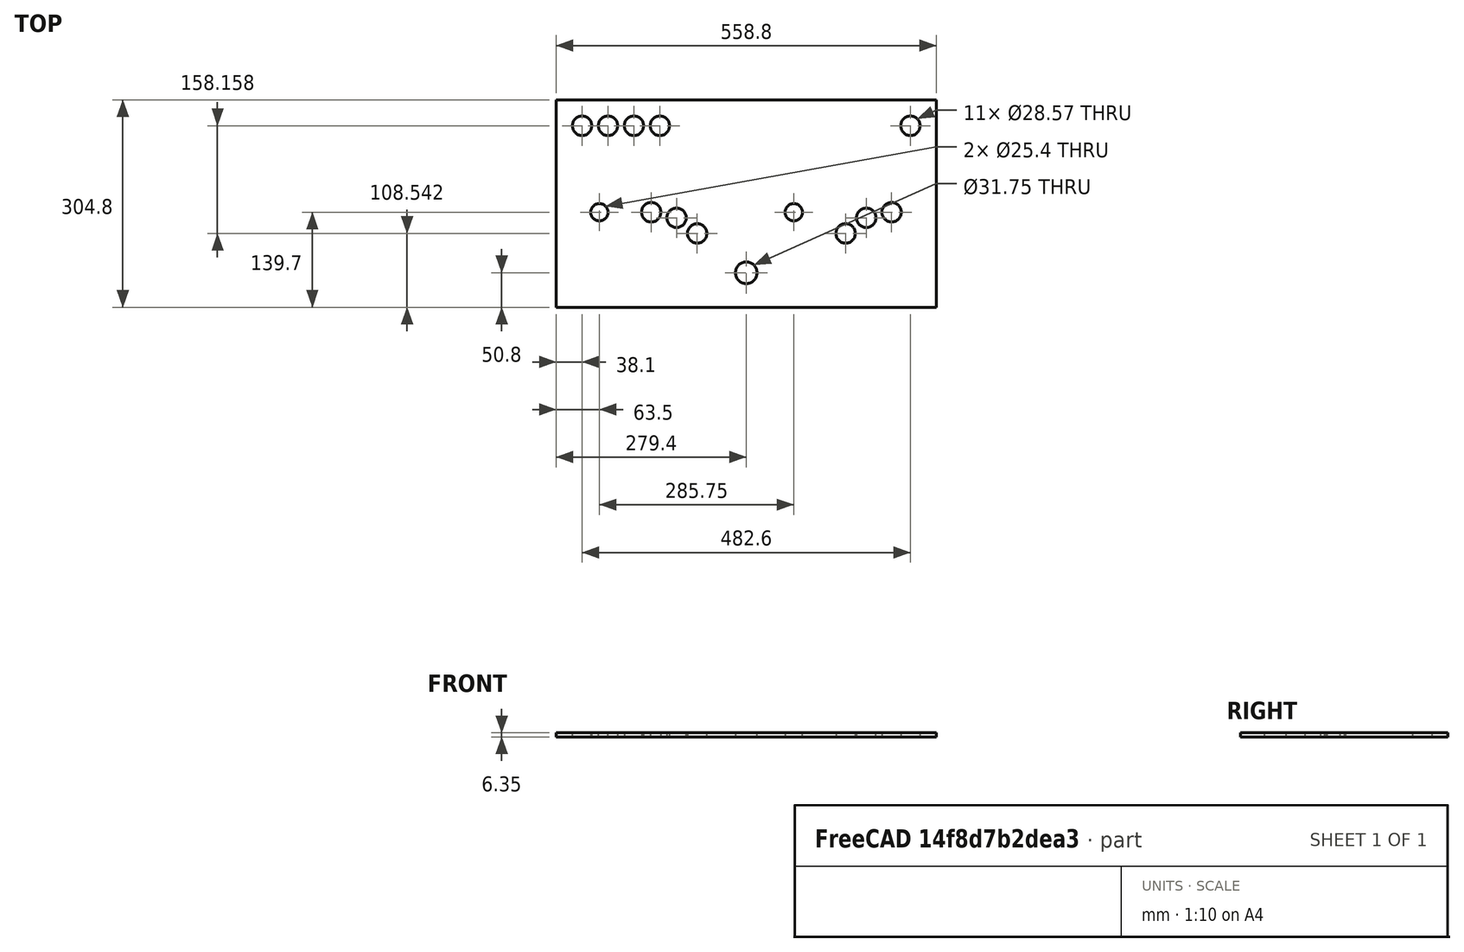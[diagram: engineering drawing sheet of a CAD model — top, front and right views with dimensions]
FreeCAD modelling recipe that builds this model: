
FCSTD DOCUMENT  (FreeCAD 0.18R16146 (Git))
Label: arcade_cabinet
License: All rights reserved
LicenseURL: http://en.wikipedia.org/wiki/All_rights_reserved
objects: Drawing::FeatureViewPython×33, Sketcher::SketchObject×1, PartDesign::Pad×1, PartDesign::Body×1, Drawing::FeatureViewPart×1, Drawing::FeaturePage×1, App::DocumentObjectGroup×1
note: 4 computed .brp shape members not serialized (recipe doc carries the construction recipe); baked Part::Feature solids carry a one-line shape summary decoded from their .brp

FEATURE [Sketcher::SketchObject] Sketch  label="Control Panel Sketch"
  MapMode = 5
  Support = -> [XY_Plane]
  sketch-geometry (20):
    g0: LineSegment StartX=-279.4 StartY=152.4 StartZ=0 EndX=279.4 EndY=152.4 EndZ=0
    g1: LineSegment StartX=279.4 StartY=152.4 StartZ=0 EndX=279.4 EndY=-152.4 EndZ=0
    g2: LineSegment StartX=279.4 StartY=-152.4 StartZ=0 EndX=-279.4 EndY=-152.4 EndZ=0
    g3: LineSegment StartX=-279.4 StartY=-152.4 StartZ=0 EndX=-279.4 EndY=152.4 EndZ=0
    g4: Circle CenterX=-241.3 CenterY=114.3 CenterZ=0 NormalX=0 NormalY=0 NormalZ=1 AngleXU=0 Radius=14.2875
    g5: Circle CenterX=-203.2 CenterY=114.3 CenterZ=0 NormalX=0 NormalY=0 NormalZ=1 AngleXU=0 Radius=14.2875
    g6: Circle CenterX=-127 CenterY=114.3 CenterZ=0 NormalX=0 NormalY=0 NormalZ=1 AngleXU=0 Radius=14.2875
    g7: Circle CenterX=-165.1 CenterY=114.3 CenterZ=0 NormalX=0 NormalY=0 NormalZ=1 AngleXU=0 Radius=14.2875
    g8: Circle CenterX=241.3 CenterY=114.3 CenterZ=0 NormalX=0 NormalY=0 NormalZ=1 AngleXU=0 Radius=14.2875
    g9: Circle CenterX=0 CenterY=-101.6 CenterZ=0 NormalX=0 NormalY=0 NormalZ=1 AngleXU=0 Radius=15.875
    g10: Circle CenterX=-215.9 CenterY=-12.7 CenterZ=0 NormalX=0 NormalY=0 NormalZ=1 AngleXU=0 Radius=12.7
    g11: Circle CenterX=69.85 CenterY=-12.7 CenterZ=0 NormalX=0 NormalY=0 NormalZ=1 AngleXU=0 Radius=12.7
    g12: Circle CenterX=-139.7 CenterY=-12.7 CenterZ=0 NormalX=0 NormalY=0 NormalZ=1 AngleXU=0 Radius=14.2875
    g13: Circle CenterX=-102.485 CenterY=-20.8643 CenterZ=0 NormalX=0 NormalY=0 NormalZ=1 AngleXU=0 Radius=14.2875
    g14: Circle CenterX=-72.1055 CenterY=-43.8576 CenterZ=0 NormalX=0 NormalY=0 NormalZ=1 AngleXU=0 Radius=14.2875
    g15: ArcOfCircle [constr] CenterX=-139.7 CenterY=-101.6 CenterZ=0 NormalX=0 NormalY=0 NormalZ=1 AngleXU=0 Radius=88.9 StartAngle=0.706954 EndAngle=1.5708
    g16: Circle CenterX=146.05 CenterY=-43.8576 CenterZ=0 NormalX=0 NormalY=0 NormalZ=1 AngleXU=0 Radius=14.2875
    g17: Circle CenterX=176.43 CenterY=-20.8643 CenterZ=0 NormalX=0 NormalY=0 NormalZ=1 AngleXU=0 Radius=14.2875
    g18: Circle CenterX=213.645 CenterY=-12.7 CenterZ=0 NormalX=0 NormalY=0 NormalZ=1 AngleXU=0 Radius=14.2875
    g19: ArcOfCircle [constr] CenterX=213.645 CenterY=-101.6 CenterZ=0 NormalX=0 NormalY=0 NormalZ=1 AngleXU=0 Radius=88.9 StartAngle=1.5708 EndAngle=2.43464
  constraints (60):
    c: Coincident(g0,g1)
    c: Coincident(g1,g2)
    c: Coincident(g2,g3)
    c: Coincident(g3,g0)
    c: Horizontal(g0)
    c: Vertical(g1)
    c: Vertical(g3)
    c: Equal(g1,g3)
    c: DistanceX(g0,g0) = 558.8  'Panel Length'
    c: DistanceY(g1,g1) = 304.8  'Panel Width'
    c: Distance(g-1,g1) = 279.4
    c: Distance(g-1,g0) = 152.4
    c: Diameter(g4) = 28.575  'PButton Diameter 1'
    c: Equal(g4,g5) = 28.575  'PButton Diameter 2'
    c: Equal(g4,g7) = 28.575  'PButton Diameter 3'
    c: Equal(g7,g6) = 28.575  'PButton Diameter 4'
    c: DistanceX(g4,g5) = 38.1  'PButton HAlign 1'
    c: DistanceX(g5,g7) = 38.1  'PButton HAlign 2'
    c: DistanceX(g7,g6) = 38.1  'PButton HAlign 3'
    c: DistanceY(g4,g5) = 0  'PButton VAlign 1'
    c: DistanceY(g6,g5) = 0  'PButton VAlign 2'
    c: DistanceY(g7,g6) = 0  'PButton VAlign 3'
    c: DistanceY(g4,g0) = 38.1  'PButtons from Top'
    c: DistanceX(g0,g4) = 38.1  'PButtons from Left'
    c: Diameter(g8) = 28.575  'Tab Button Diameter'
    c: DistanceY(g8,g0) = 38.1  'Tab from Top'
    c: DistanceX(g8,g0) = 38.1  'Tab from Right'
    c: PointOnObject(g9,g-2)  'SPNR_CNTR'
    c: Diameter(g9) = 31.75  'SPNR_Diam'
    c: Diameter(g10) = 25.4  'JSTK1_Diam'
    c: DistanceX(g0,g10) = 63.5  'JSTK1_HDist'
    c: DistanceY(g2,g10) = 139.7  'JSTK1_VDist'
    c: DistanceY(g2,g9) = 50.8  'SPNR_VDist'
    c: DistanceY(g11,g10) = 0  'JSTK2_VAlign'
    c: DistanceX(g11,g1) = 209.55  'JSTK2_HDist'
    c: Diameter(g11) = 25.4  'JSTK2_Diam'
    c: Diameter(g12) = 28.575  'P1_Button1_Diam'
    c: DistanceX(g10,g12) = 76.2  'P1_Button1_to_JSTK1_HDist'
    c: DistanceY(g12,g10) = 0  'P1_Button1_to_JSTK1_VDist'
    c: Equal(g13,g12)  'P1_Button2_Diam'
    c: Equal(g12,g14)  'P1_Button3_Diam'
    c: Coincident(g15,g12)  'P1_Button1_Center'
    c: Coincident(g15,g14)  'P1_Button3_Center'
    c: DistanceX(g12,g15) = 0  'P1_Button_to_Arc_Center'
    c: DistanceY(g2,g15) = 50.8  'Arc_Center_to_Panel_Bottom'
    c: PointOnObject(g13,g15)  'P1_Button2_Arc'
    c: Distance(g13,g12) = 38.1  'P1_Button1_to_P1_Button2'
    c: Distance(g14,g13) = 38.1  'P1_Button2_to_P1_Button3'
    c: Diameter(g16) = 28.575  'P1_Button1_Diam'
    c: Equal(g17,g16)  'P1_Button2_Diam'
    c: Equal(g16,g18)  'P1_Button3_Diam'
    c: Coincident(g19,g16)  'P2_Button1_Center'
    c: Coincident(g19,g18)  'P2_Button3_Center'
    c: PointOnObject(g17,g19)  'P2_Button2_Arc'
    c: Distance(g17,g16) = 38.1  'P2_Button1_to_P2_Button2'
    c: Distance(g18,g17) = 38.1  'P2_Button2_to_P2_Button3'
    c: DistanceY(g1,g19) = 50.8  'P2_Button_Arc_Vdist'
    c: DistanceX(g19,g18) = 0  'P2_Button3_to_Arc_Center_HDist'
    c: DistanceX(g11,g16) = 76.2  'P2_Button1_to_JSTK2_Hdist'
    c: DistanceY(g18,g11) = 0  'P2_Button3_to_JSTK2_Vdist'
FEATURE [PartDesign::Pad] Pad  label="Control Panel Pad"
  Length = 6.35
  Length2 = 100.076
  Profile = -> Sketch
  Type = 0
FEATURE [PartDesign::Body] Body  label="Control Panel Body"
  Group = -> [Sketch,Pad]
  Origin = -> Origin
  Tip = -> Pad
FEATURE [Drawing::FeatureViewPart] Ortho  label="Control Panel Ortho View"
  Direction = (0,0,1)
  HiddenWidth = 0.15
  LineWidth = 0.35
  Rotation = 0
  Scale = 0.25
  ShowHiddenLines = false
  ShowSmoothLines = false
  Source = -> Body
  Tolerance = 0.05
  ViewResult = <g id="Control Panel Ortho View"\n   transform="rotate(0,148.5,81.5) translate(148.5,81.5) scale(0.25,0.25)"\n  >\n<g   fill="none"\n   stroke="rgb(0, 0, 0)"\n   stroke-linecap="butt"\n   stroke-linejoin="miter"\n   stroke-width="1.400000"\n   transform="scale(1,-1)"\n  >\n<path id= "1" d=" M -279.4 152.4 L 279.4 152.4 " />\n<path id= "2" d=" M 279.4 152.4 L 279.4 -152.4 " />\n<path id= "3" d=" M 279.4 -152.4 L -279.4 -152.4 " />\n<path id= "4" d=" M -279.4 -152.4 L -279.4 152.4 " />\n<circle cx ="0" cy ="-101.6" r ="15.875" /><circle cx ="-72.1055" cy ="-43.8576" r ="14.2875" /><circle cx ="146.05" cy ="-43.8576" r ="14.2875" /><circle cx ="176.43" cy ="-20.8643" r ="14.2875" /><circle cx ="-102.485" cy ="-20.8643" r ="14.2875" /><circle cx ="-139.7" cy ="-12.7" r ="14.2875" /><circle cx ="213.645" cy ="-12.7" r ="14.2875" /><circle cx ="-127" cy ="114.3" r ="14.2875" /><circle cx ="241.3" cy ="114.3" r ="14.2875" /><circle cx ="-165.1" cy ="114.3" r ="14.2875" /><circle cx ="-241.3" cy ="114.3" r ="14.2875" /><circle cx ="-203.2" cy ="114.3" r ="14.2875" /><circle cx ="69.85" cy ="-12.7" r ="12.7" /><circle cx ="-215.9" cy ="-12.7" r ="12.7" /></g>\n</g>
  Visible = true
  X = 148.5
  Y = 81.5
FEATURE [Drawing::FeatureViewPython] dim001  label="Panel Width"  # drawing view (typed FeaturePython)
  Rotation = 0
  ViewResult = <g> \n  <line x1="76.650000" y1="119.600000" x2="57.586698" y2="119.600000" style="stroke:rgb(0,0,255);stroke-width:0.50" />\n<line x1="76.650000" y1="43.400000" x2="57.586698" y2="43.400000" style="stroke:rgb(0,0,255);stroke-width:0.50" />\n<line x1="58.586698" y1="119.600000" x2="58.586698" y2="43.400000" style="stroke:rgb(0,0,255);stroke-width:0.50" /> \n  <polygon points="58.586698,43.400000 57.586698,44.900000 58.586698,45.400000 59.586698,44.900000" style="fill:rgb(0,0,255);stroke:rgb(0,0,255);stroke-width:0" /><polygon points="58.586698,119.600000 59.586698,118.100000 58.586698,117.600000 57.586698,118.100000" style="fill:rgb(0,0,255);stroke:rgb(0,0,255);stroke-width:0" /> \n  <text x="56.586698" y="81.500000" font-family="inherit" font-size="3.6" fill="rgb(0,0,255)" text-anchor="middle" transform="rotate(-90.000000 56.586698,81.500000)" >12</text> </g>
  Visible = true
  X = 0
  Y = 0
  arrowL1 = 1.5
  arrowL2 = 0.5
  arrowW = 2
  arrow_scheme = 0
  autoPlaceOffset = 2
  autoPlaceText = true
  click1_x = 58.5867
  click1_y = 76.756
  click2_x = 58.5867
  click2_y = 76.756
  comma_decimal_place = false
  dimension_line_overshoot = 1
  gap_datum_points = 2
  halfDimension_linear = false
  lineColor = rgb(0,0,255)
  strokeWidth = 0.5
  textFormat_linear = %(value)3.3f
  textRenderer_color = rgb(0,0,255)
  textRenderer_family = inherit
  textRenderer_size = 3.6
  unit_custom_scale = 1
  unit_scheme = 2
FEATURE [Drawing::FeatureViewPython] dim002  label="Panel Length"  # drawing view (typed FeaturePython)
  Rotation = 0
  ViewResult = <g> \n  <line x1="78.650000" y1="41.400000" x2="78.650000" y2="26.439340" style="stroke:rgb(0,0,255);stroke-width:0.50" />\n<line x1="218.350000" y1="41.400000" x2="218.350000" y2="26.439340" style="stroke:rgb(0,0,255);stroke-width:0.50" />\n<line x1="78.650000" y1="27.439340" x2="218.350000" y2="27.439340" style="stroke:rgb(0,0,255);stroke-width:0.50" /> \n  <polygon points="218.350000,27.439340 216.850000,26.439340 216.350000,27.439340 216.850000,28.439340" style="fill:rgb(0,0,255);stroke:rgb(0,0,255);stroke-width:0" /><polygon points="78.650000,27.439340 80.150000,28.439340 80.650000,27.439340 80.150000,26.439340" style="fill:rgb(0,0,255);stroke:rgb(0,0,255);stroke-width:0" /> \n  <text x="148.500000" y="25.439340" font-family="inherit" font-size="3.6" fill="rgb(0,0,255)" text-anchor="middle" transform="rotate(0.000000 148.500000,25.439340)" >22</text> </g>
  Visible = true
  X = 0
  Y = 0
  arrowL1 = 1.5
  arrowL2 = 0.5
  arrowW = 2
  arrow_scheme = 0
  autoPlaceOffset = 2
  autoPlaceText = true
  click1_x = 102.712
  click1_y = 27.4393
  click2_x = 102.712
  click2_y = 27.4393
  comma_decimal_place = false
  dimension_line_overshoot = 1
  gap_datum_points = 2
  halfDimension_linear = false
  lineColor = rgb(0,0,255)
  strokeWidth = 0.5
  textFormat_linear = %(value)3.3f
  textRenderer_color = rgb(0,0,255)
  textRenderer_family = inherit
  textRenderer_size = 3.6
  unit_custom_scale = 1
  unit_scheme = 2
FEATURE [Drawing::FeatureViewPython] dim004  label="Coin Button HDist to Panel Edge"  # drawing view (typed FeaturePython)
  Rotation = 0
  ViewResult = <g> \n  <line x1="88.175000" y1="58.496875" x2="88.175000" y2="64.914175" style="stroke:rgb(0,0,255);stroke-width:0.50" />\n<line x1="78.650000" y1="45.400000" x2="78.650000" y2="64.914175" style="stroke:rgb(0,0,255);stroke-width:0.50" />\n<line x1="88.175000" y1="63.914175" x2="78.650000" y2="63.914175" style="stroke:rgb(0,0,255);stroke-width:0.50" /> \n  <polygon points="78.650000,63.914175 80.150000,64.914175 80.650000,63.914175 80.150000,62.914175" style="fill:rgb(0,0,255);stroke:rgb(0,0,255);stroke-width:0" /><polygon points="88.175000,63.914175 86.675000,62.914175 86.175000,63.914175 86.675000,64.914175" style="fill:rgb(0,0,255);stroke:rgb(0,0,255);stroke-width:0" /> \n  <text x="83.412500" y="61.914175" font-family="inherit" font-size="3.6" fill="rgb(0,0,255)" text-anchor="middle" transform="rotate(0.000000 83.412500,61.914175)" >1.5</text> </g>
  Visible = true
  X = 0
  Y = 0
  arrowL1 = 1.5
  arrowL2 = 0.5
  arrowW = 2
  arrow_scheme = 0
  autoPlaceOffset = 2
  autoPlaceText = true
  click1_x = 85.5208
  click1_y = 63.9142
  click2_x = 85.5208
  click2_y = 63.9142
  comma_decimal_place = false
  dimension_line_overshoot = 1
  gap_datum_points = 2
  halfDimension_linear = false
  lineColor = rgb(0,0,255)
  strokeWidth = 0.5
  textFormat_linear = %(value)3.3f
  textRenderer_color = rgb(0,0,255)
  textRenderer_family = inherit
  textRenderer_size = 3.6
  unit_custom_scale = 1
  unit_scheme = 2
FEATURE [Drawing::FeatureViewPython] dim005  label="Coin Button VDist to Panel Edge"  # drawing view (typed FeaturePython)
  Rotation = 0
  ViewResult = <g> \n  <line x1="82.603125" y1="52.925000" x2="70.422058" y2="52.925000" style="stroke:rgb(0,0,255);stroke-width:0.50" />\n<line x1="76.650000" y1="43.400000" x2="70.422058" y2="43.400000" style="stroke:rgb(0,0,255);stroke-width:0.50" />\n<line x1="71.422058" y1="52.925000" x2="71.422058" y2="43.400000" style="stroke:rgb(0,0,255);stroke-width:0.50" /> \n  <polygon points="71.422058,43.400000 70.422058,44.900000 71.422058,45.400000 72.422058,44.900000" style="fill:rgb(0,0,255);stroke:rgb(0,0,255);stroke-width:0" /><polygon points="71.422058,52.925000 72.422058,51.425000 71.422058,50.925000 70.422058,51.425000" style="fill:rgb(0,0,255);stroke:rgb(0,0,255);stroke-width:0" /> \n  <text x="69.422058" y="48.162500" font-family="inherit" font-size="3.6" fill="rgb(0,0,255)" text-anchor="middle" transform="rotate(-90.000000 69.422058,48.162500)" >1.5</text> </g>
  Visible = true
  X = 0
  Y = 0
  arrowL1 = 1.5
  arrowL2 = 0.5
  arrowW = 2
  arrow_scheme = 0
  autoPlaceOffset = 2
  autoPlaceText = true
  click1_x = 71.4221
  click1_y = 52.2878
  click2_x = 71.4221
  click2_y = 52.2878
  comma_decimal_place = false
  dimension_line_overshoot = 1
  gap_datum_points = 2
  halfDimension_linear = false
  lineColor = rgb(0,0,255)
  strokeWidth = 0.5
  textFormat_linear = %(value)3.3f
  textRenderer_color = rgb(0,0,255)
  textRenderer_family = inherit
  textRenderer_size = 3.6
  unit_custom_scale = 1
  unit_scheme = 2
FEATURE [Drawing::FeatureViewPython] dim006  label="Coin Button to P1 Button HDist"  # drawing view (typed FeaturePython)
  Rotation = 0
  ViewResult = <g> \n  <line x1="88.175000" y1="54.925000" x2="88.175000" y2="64.996578" style="stroke:rgb(0,0,255);stroke-width:0.50" />\n<line x1="97.700000" y1="54.925000" x2="97.700000" y2="64.996578" style="stroke:rgb(0,0,255);stroke-width:0.50" />\n<line x1="88.175000" y1="63.996578" x2="97.700000" y2="63.996578" style="stroke:rgb(0,0,255);stroke-width:0.50" /> \n  <polygon points="97.700000,63.996578 96.200000,62.996578 95.700000,63.996578 96.200000,64.996578" style="fill:rgb(0,0,255);stroke:rgb(0,0,255);stroke-width:0" /><polygon points="88.175000,63.996578 89.675000,64.996578 90.175000,63.996578 89.675000,62.996578" style="fill:rgb(0,0,255);stroke:rgb(0,0,255);stroke-width:0" /> \n  <text x="92.937500" y="61.996578" font-family="inherit" font-size="3.6" fill="rgb(0,0,255)" text-anchor="middle" transform="rotate(0.000000 92.937500,61.996578)" >1.5</text> </g>
  Visible = true
  X = 0
  Y = 0
  arrowL1 = 1.5
  arrowL2 = 0.5
  arrowW = 2
  arrow_scheme = 0
  autoPlaceOffset = 2
  autoPlaceText = true
  click1_x = 98.1851
  click1_y = 63.9966
  click2_x = 98.1851
  click2_y = 63.9966
  comma_decimal_place = false
  dimension_line_overshoot = 1
  gap_datum_points = 2
  halfDimension_linear = false
  lineColor = rgb(0,0,255)
  strokeWidth = 0.5
  textFormat_linear = %(value)3.3f
  textRenderer_color = rgb(0,0,255)
  textRenderer_family = inherit
  textRenderer_size = 3.6
  unit_custom_scale = 1
  unit_scheme = 2
FEATURE [Drawing::FeatureViewPython] dim008  label="JSTK1 HDist to Panel"  # drawing view (typed FeaturePython)
  Rotation = 0
  ViewResult = <g> \n  <line x1="94.525000" y1="89.850000" x2="94.525000" y2="100.695034" style="stroke:rgb(0,0,255);stroke-width:0.50" />\n<line x1="78.650000" y1="117.600000" x2="78.650000" y2="98.695034" style="stroke:rgb(0,0,255);stroke-width:0.50" />\n<line x1="94.525000" y1="99.695034" x2="78.650000" y2="99.695034" style="stroke:rgb(0,0,255);stroke-width:0.50" /> \n  <polygon points="78.650000,99.695034 80.150000,100.695034 80.650000,99.695034 80.150000,98.695034" style="fill:rgb(0,0,255);stroke:rgb(0,0,255);stroke-width:0" /><polygon points="94.525000,99.695034 93.025000,98.695034 92.525000,99.695034 93.025000,100.695034" style="fill:rgb(0,0,255);stroke:rgb(0,0,255);stroke-width:0" /> \n  <text x="86.587500" y="97.695034" font-family="inherit" font-size="3.6" fill="rgb(0,0,255)" text-anchor="middle" transform="rotate(0.000000 86.587500,97.695034)" >2.5</text> </g>
  Visible = true
  X = 0
  Y = 0
  arrowL1 = 1.5
  arrowL2 = 0.5
  arrowW = 2
  arrow_scheme = 0
  autoPlaceOffset = 2
  autoPlaceText = true
  click1_x = 85.952
  click1_y = 99.695
  click2_x = 85.952
  click2_y = 99.695
  comma_decimal_place = false
  dimension_line_overshoot = 1
  gap_datum_points = 2
  halfDimension_linear = false
  lineColor = rgb(0,0,255)
  strokeWidth = 0.5
  textFormat_linear = %(value)3.3f
  textRenderer_color = rgb(0,0,255)
  textRenderer_family = inherit
  textRenderer_size = 3.6
  unit_custom_scale = 1
  unit_scheme = 2
FEATURE [Drawing::FeatureViewPython] dim009  label="JSTK1 VDist to Panel"  # drawing view (typed FeaturePython)
  Rotation = 0
  ViewResult = <g> \n  <line x1="89.350000" y1="84.675000" x2="68.879697" y2="84.675000" style="stroke:rgb(0,0,255);stroke-width:0.50" />\n<line x1="76.650000" y1="119.600000" x2="68.879697" y2="119.600000" style="stroke:rgb(0,0,255);stroke-width:0.50" />\n<line x1="69.879697" y1="84.675000" x2="69.879697" y2="119.600000" style="stroke:rgb(0,0,255);stroke-width:0.50" /> \n  <polygon points="69.879697,119.600000 70.879697,118.100000 69.879697,117.600000 68.879697,118.100000" style="fill:rgb(0,0,255);stroke:rgb(0,0,255);stroke-width:0" /><polygon points="69.879697,84.675000 68.879697,86.175000 69.879697,86.675000 70.879697,86.175000" style="fill:rgb(0,0,255);stroke:rgb(0,0,255);stroke-width:0" /> \n  <text x="67.879697" y="102.137500" font-family="inherit" font-size="3.6" fill="rgb(0,0,255)" text-anchor="middle" transform="rotate(-90.000000 67.879697,102.137500)" >5.5</text> </g>
  Visible = true
  X = 0
  Y = 0
  arrowL1 = 1.5
  arrowL2 = 0.5
  arrowW = 2
  arrow_scheme = 0
  autoPlaceOffset = 2
  autoPlaceText = true
  click1_x = 69.8797
  click1_y = 94.1047
  click2_x = 69.8797
  click2_y = 94.1047
  comma_decimal_place = false
  dimension_line_overshoot = 1
  gap_datum_points = 2
  halfDimension_linear = false
  lineColor = rgb(0,0,255)
  strokeWidth = 0.5
  textFormat_linear = %(value)3.3f
  textRenderer_color = rgb(0,0,255)
  textRenderer_family = inherit
  textRenderer_size = 3.6
  unit_custom_scale = 1
  unit_scheme = 2
FEATURE [Drawing::FeatureViewPython] dim010  label="P1 Button1 to JSTK1 HDist"  # drawing view (typed FeaturePython)
  Rotation = 0
  ViewResult = <g> \n  <line x1="94.525000" y1="86.675000" x2="94.525000" y2="100.684233" style="stroke:rgb(0,0,255);stroke-width:0.50" />\n<line x1="113.575000" y1="86.675000" x2="113.575000" y2="100.684233" style="stroke:rgb(0,0,255);stroke-width:0.50" />\n<line x1="94.525000" y1="99.684233" x2="113.575000" y2="99.684233" style="stroke:rgb(0,0,255);stroke-width:0.50" /> \n  <polygon points="113.575000,99.684233 112.075000,98.684233 111.575000,99.684233 112.075000,100.684233" style="fill:rgb(0,0,255);stroke:rgb(0,0,255);stroke-width:0" /><polygon points="94.525000,99.684233 96.025000,100.684233 96.525000,99.684233 96.025000,98.684233" style="fill:rgb(0,0,255);stroke:rgb(0,0,255);stroke-width:0" /> \n  <text x="104.050000" y="97.684233" font-family="inherit" font-size="3.6" fill="rgb(0,0,255)" text-anchor="middle" transform="rotate(0.000000 104.050000,97.684233)" >3</text> </g>
  Visible = true
  X = 0
  Y = 0
  arrowL1 = 1.5
  arrowL2 = 0.5
  arrowW = 2
  arrow_scheme = 0
  autoPlaceOffset = 2
  autoPlaceText = true
  click1_x = 113.952
  click1_y = 99.6842
  click2_x = 113.952
  click2_y = 99.6842
  comma_decimal_place = false
  dimension_line_overshoot = 1
  gap_datum_points = 2
  halfDimension_linear = false
  lineColor = rgb(0,0,255)
  strokeWidth = 0.5
  textFormat_linear = %(value)3.3f
  textRenderer_color = rgb(0,0,255)
  textRenderer_family = inherit
  textRenderer_size = 3.6
  unit_custom_scale = 1
  unit_scheme = 2
FEATURE [Drawing::FeatureViewPython] dia001  label="Coin Button Diameter"  # drawing view (typed FeaturePython)
  Rotation = 0
  ViewResult = <g>  <circle cx ="88.175000" cy ="52.925000" r="0.250000" stroke="none" fill="rgb(0,0,255)" /> \n<line x1="88.001472" y1="40.209550" x2="88.223741" y2="56.496542" style="stroke:rgb(0,0,255);stroke-width:0.50" />\n<polygon points="88.126259,49.353458 87.146821,50.866964 88.153551,51.353271 89.146635,50.839672" style="fill:rgb(0,0,255);stroke:rgb(0,0,255);stroke-width:0" />\n<polygon points="88.223741,56.496542 89.203179,54.983036 88.196449,54.496729 87.203365,55.010328" style="fill:rgb(0,0,255);stroke:rgb(0,0,255);stroke-width:0" />\n<line x1="88.001472" y1="40.209550" x2="96.962458" y2="40.209550" style="stroke:rgb(0,0,255);stroke-width:0.50" />\n<text x="92.481965" y="38.209550" font-family="inherit" font-size="3.6" fill="rgb(0,0,255)" text-anchor="middle" transform="rotate(0.000000 92.481965,38.209550)" >Ø1.125</text> </g>
  Visible = true
  X = 0
  Y = 0
  arrowL1 = 1.5
  arrowL2 = 0.5
  arrowW = 2
  arrow_scheme = 0
  autoPlaceOffset = 2
  autoPlaceText = true
  centerPointDia = 0.5
  click1_x = 88.0015
  click1_y = 40.2095
  click2_x = 96.9625
  click2_y = 40.4393
  click3_x = 96.9625
  click3_y = 40.4393
  comma_decimal_place = false
  lineColor = rgb(0,0,255)
  strokeWidth = 0.5
  textFormat_circular = Ø%(value)3.3f
  textRenderer_color = rgb(0,0,255)
  textRenderer_family = inherit
  textRenderer_size = 3.6
  unit_custom_scale = 1
  unit_scheme = 2
FEATURE [Drawing::FeatureViewPython] dia002  label="JSTK1 Diameter"  # drawing view (typed FeaturePython)
  Rotation = 0
  ViewResult = <g>  <circle cx ="94.525000" cy ="84.675000" r="0.250000" stroke="none" fill="rgb(0,0,255)" /> \n<line x1="94.894538" y1="77.891643" x2="94.352291" y2="87.845299" style="stroke:rgb(0,0,255);stroke-width:0.50" />\n<polygon points="94.697709,81.504701 93.617595,82.948083 94.588916,83.501740 95.614634,83.056876" style="fill:rgb(0,0,255);stroke:rgb(0,0,255);stroke-width:0" />\n<polygon points="94.352291,87.845299 95.432405,86.401917 94.461084,85.848260 93.435366,86.293124" style="fill:rgb(0,0,255);stroke:rgb(0,0,255);stroke-width:0" />\n<line x1="94.894538" y1="77.891643" x2="99.260146" y2="77.891643" style="stroke:rgb(0,0,255);stroke-width:0.50" />\n<text x="97.077342" y="75.891643" font-family="inherit" font-size="3.6" fill="rgb(0,0,255)" text-anchor="middle" transform="rotate(0.000000 97.077342,75.891643)" >Ø1</text> </g>
  Visible = true
  X = 0
  Y = 0
  arrowL1 = 1.5
  arrowL2 = 0.5
  arrowW = 2
  arrow_scheme = 0
  autoPlaceOffset = 2
  autoPlaceText = true
  centerPointDia = 0.5
  click1_x = 94.8945
  click1_y = 77.8916
  click2_x = 99.2601
  click2_y = 78.1214
  click3_x = 99.2601
  click3_y = 78.1214
  comma_decimal_place = false
  lineColor = rgb(0,0,255)
  strokeWidth = 0.5
  textFormat_circular = Ø%(value)3.3f
  textRenderer_color = rgb(0,0,255)
  textRenderer_family = inherit
  textRenderer_size = 3.6
  unit_custom_scale = 1
  unit_scheme = 2
FEATURE [Drawing::FeatureViewPython] dia003  label="P1 Button1 Diameter"  # drawing view (typed FeaturePython)
  Rotation = 0
  ViewResult = <g>  <circle cx ="113.575000" cy ="84.675000" r="0.250000" stroke="none" fill="rgb(0,0,255)" /> \n<line x1="113.590548" y1="77.646686" x2="113.567098" y2="88.246866" style="stroke:rgb(0,0,255);stroke-width:0.50" />\n<polygon points="113.582902,81.103134 112.579586,82.600918 113.578477,83.103129 114.579581,82.605342" style="fill:rgb(0,0,255);stroke:rgb(0,0,255);stroke-width:0" />\n<polygon points="113.567098,88.246866 114.570414,86.749082 113.571523,86.246871 112.570419,86.744658" style="fill:rgb(0,0,255);stroke:rgb(0,0,255);stroke-width:0" />\n<line x1="113.590548" y1="77.646686" x2="118.158000" y2="77.646686" style="stroke:rgb(0,0,255);stroke-width:0.50" />\n<text x="115.874274" y="75.646686" font-family="inherit" font-size="3.6" fill="rgb(0,0,255)" text-anchor="middle" transform="rotate(0.000000 115.874274,75.646686)" >Ø1.125</text> </g>
  Visible = true
  X = 0
  Y = 0
  arrowL1 = 1.5
  arrowL2 = 0.5
  arrowW = 2
  arrow_scheme = 0
  autoPlaceOffset = 2
  autoPlaceText = true
  centerPointDia = 0.5
  click1_x = 113.591
  click1_y = 77.6467
  click2_x = 118.158
  click2_y = 78.0439
  click3_x = 118.158
  click3_y = 78.0439
  comma_decimal_place = false
  lineColor = rgb(0,0,255)
  strokeWidth = 0.5
  textFormat_circular = Ø%(value)3.3f
  textRenderer_color = rgb(0,0,255)
  textRenderer_family = inherit
  textRenderer_size = 3.6
  unit_custom_scale = 1
  unit_scheme = 2
FEATURE [Drawing::FeatureViewPython] dimStack001  label="P1 Button1 to P1 Button3"  # drawing view (typed FeaturePython)
  Rotation = 0
  ViewResult = <g> <line x1="113.575000" y1="86.675001" x2="113.575000" y2="110.228830" style="stroke:rgb(0,0,255);stroke-width:0.50" />\n<line x1="130.473625" y1="94.464401" x2="130.473625" y2="110.228830" style="stroke:rgb(0,0,255);stroke-width:0.50" />\n<line x1="113.575000" y1="109.228830" x2="130.473625" y2="109.228830" style="stroke:rgb(0,0,255);stroke-width:0.50" />\n<polygon points="113.575000,109.228830 115.075000,110.228830 115.575000,109.228830 115.075000,108.228830" style="fill:rgb(0,0,255);stroke:rgb(0,0,255);stroke-width:0" />\n<polygon points="130.473625,109.228830 128.973625,108.228830 128.473625,109.228830 128.973625,110.228830" style="fill:rgb(0,0,255);stroke:rgb(0,0,255);stroke-width:0" />\n<text x="122.024313" y="107.228830" font-family="inherit" font-size="3.6" fill="rgb(0,0,255)" text-anchor="middle" transform="rotate(0.000000 122.024313,107.228830)" >2.661</text> </g> 
  Visible = true
  X = 0
  Y = 0
  arrowL1 = 1.5
  arrowL2 = 0.5
  arrowW = 2
  arrow_scheme = 0
  autoPlaceOffset = 2
  click1_x = 117.672
  click1_y = 109.229
  comma_decimal_place = false
  dimension_line_overshoot = 1
  gap_datum_points = 2
  lineColor = rgb(0,0,255)
  stack_offset = 7
  stack_offset0 = 0
  strokeWidth = 0.5
  textFormat_linear = %(value)3.3f
  textRenderer_color = rgb(0,0,255)
  textRenderer_family = inherit
  textRenderer_size = 3.6
  unit_custom_scale = 1
  unit_scheme = 2
FEATURE [Drawing::FeatureViewPython] dimStack002  label="P1 Button1 to P1 Button2"  # drawing view (typed FeaturePython)
  Rotation = 0
  ViewResult = <g> <line x1="122.878750" y1="88.716076" x2="122.878750" y2="100.730671" style="stroke:rgb(0,0,255);stroke-width:0.50" />\n<line x1="113.575000" y1="86.675001" x2="113.575000" y2="100.730671" style="stroke:rgb(0,0,255);stroke-width:0.50" />\n<line x1="122.878750" y1="99.730671" x2="113.575000" y2="99.730671" style="stroke:rgb(0,0,255);stroke-width:0.50" />\n<polygon points="122.878750,99.730671 121.378750,98.730671 120.878750,99.730671 121.378750,100.730671" style="fill:rgb(0,0,255);stroke:rgb(0,0,255);stroke-width:0" />\n<polygon points="113.575000,99.730671 115.075000,100.730671 115.575000,99.730671 115.075000,98.730671" style="fill:rgb(0,0,255);stroke:rgb(0,0,255);stroke-width:0" />\n<text x="118.226875" y="97.730671" font-family="inherit" font-size="3.6" fill="rgb(0,0,255)" text-anchor="middle" transform="rotate(0.000000 118.226875,97.730671)" >1.465</text> </g> 
  Visible = true
  X = 0
  Y = 0
  arrowL1 = 1.5
  arrowL2 = 0.5
  arrowW = 2
  arrow_scheme = 0
  autoPlaceOffset = 2
  click1_x = 122.157
  click1_y = 99.7307
  comma_decimal_place = false
  dimension_line_overshoot = 1
  gap_datum_points = 2
  lineColor = rgb(0,0,255)
  stack_offset = 7
  stack_offset0 = 0
  strokeWidth = 0.5
  textFormat_linear = %(value)3.3f
  textRenderer_color = rgb(0,0,255)
  textRenderer_family = inherit
  textRenderer_size = 3.6
  unit_custom_scale = 1
  unit_scheme = 2
FEATURE [Drawing::FeatureViewPython] centerLines001  label="Panel Center Left"  # drawing view (typed FeaturePython)
  Rotation = 0
  ViewResult = <g transform="scale(0.250000,0.250000)" stroke="rgb(0,0,255)"  stroke-width="1.280000" > <path d="M 314.600000,326.000000 L 326.600000,326.000000 "/>\n<path d="M 314.600000,326.000000 L 302.600000,326.000000 "/> </g> 
  Visible = true
  X = 0
  Y = 0
  centerLine_color = rgb(0,0,255)
  centerLine_len_dash = 6
  centerLine_len_dot = 3
  centerLine_len_gap = 2
  centerLine_width = 0.32
  click1_x = 81.7786
  click1_y = 81.7786
  click2_x = 74.6774
  click2_y = 81.7786
FEATURE [Drawing::FeatureViewPython] centerLines002  label="Panel Center Top"  # drawing view (typed FeaturePython)
  Rotation = 0
  ViewResult = <g transform="scale(0.250000,0.250000)" stroke="rgb(0,0,255)"  stroke-width="1.280000" > <path d="M 594.000000,173.600000 L 594.000000,161.600000 "/>\n<path d="M 594.000000,173.600000 L 594.000000,185.600000 "/> </g> 
  Visible = true
  X = 0
  Y = 0
  centerLine_color = rgb(0,0,255)
  centerLine_len_dash = 6
  centerLine_len_dot = 3
  centerLine_len_gap = 2
  centerLine_width = 0.32
  click1_x = 149.355
  click1_y = 39.8585
  click2_x = 149.126
  click2_y = 46.7306
FEATURE [Drawing::FeatureViewPython] centerLines003  label="Panel Center Bottom"  # drawing view (typed FeaturePython)
  Rotation = 0
  ViewResult = <g transform="scale(0.250000,0.250000)" stroke="rgb(0,0,255)"  stroke-width="1.280000" > <path d="M 594.000000,478.400000 L 594.000000,490.400000 "/>\n<path d="M 594.000000,478.400000 L 594.000000,466.400000 "/> </g> 
  Visible = true
  X = 0
  Y = 0
  centerLine_color = rgb(0,0,255)
  centerLine_len_dash = 6
  centerLine_len_dot = 3
  centerLine_len_gap = 2
  centerLine_width = 0.32
  click1_x = 148.99
  click1_y = 123.456
  click2_x = 149.734
  click2_y = 115.523
FEATURE [Drawing::FeatureViewPython] centerLines004  label="Panel Center Right"  # drawing view (typed FeaturePython)
  Rotation = 0
  ViewResult = <g transform="scale(0.250000,0.250000)" stroke="rgb(0,0,255)"  stroke-width="1.280000" > <path d="M 873.400000,326.000000 L 885.400000,326.000000 "/>\n<path d="M 873.400000,326.000000 L 861.400000,326.000000 "/> </g> 
  Visible = true
  X = 0
  Y = 0
  centerLine_color = rgb(0,0,255)
  centerLine_len_dash = 6
  centerLine_len_dot = 3
  centerLine_len_gap = 2
  centerLine_width = 0.32
  click1_x = 221.626
  click1_y = 81.8083
  click2_x = 214.189
  click2_y = 82.552
FEATURE [Drawing::FeatureViewPython] dim003  label="P1 Button1 to P1 Button2 VDist"  # drawing view (typed FeaturePython)
  Rotation = 0
  ViewResult = <g> \n  <line x1="115.575000" y1="84.675000" x2="140.920976" y2="84.675000" style="stroke:rgb(0,0,255);stroke-width:0.50" />\n<line x1="124.878750" y1="86.716075" x2="140.920976" y2="86.716075" style="stroke:rgb(0,0,255);stroke-width:0.50" />\n<line x1="139.920976" y1="84.675000" x2="139.920976" y2="86.716075" style="stroke:rgb(0,0,255);stroke-width:0.50" /> \n  <polygon points="139.920976,86.716075 138.920976,88.216075 139.920976,88.716075 140.920976,88.216075" style="fill:rgb(0,0,255);stroke:rgb(0,0,255);stroke-width:0" /><polygon points="139.920976,84.675000 140.920976,83.175000 139.920976,82.675000 138.920976,83.175000" style="fill:rgb(0,0,255);stroke:rgb(0,0,255);stroke-width:0" /> \n  <text x="137.920976" y="85.695538" font-family="inherit" font-size="3.6" fill="rgb(0,0,255)" text-anchor="middle" transform="rotate(-90.000000 137.920976,85.695538)" >0.321</text> </g>
  Visible = true
  X = 0
  Y = 0
  arrowL1 = 1.5
  arrowL2 = 0.5
  arrowW = 2
  arrow_scheme = 0
  autoPlaceOffset = 2
  autoPlaceText = true
  click1_x = 139.921
  click1_y = 84.8401
  click2_x = 139.921
  click2_y = 84.8401
  comma_decimal_place = false
  dimension_line_overshoot = 1
  gap_datum_points = 2
  halfDimension_linear = false
  lineColor = rgb(0,0,255)
  strokeWidth = 0.5
  textFormat_linear = %(value)3.3f
  textRenderer_color = rgb(0,0,255)
  textRenderer_family = inherit
  textRenderer_size = 3.6
  unit_custom_scale = 1
  unit_scheme = 2
FEATURE [Drawing::FeatureViewPython] dim007  label="P1 Button1 to P1 Button3 VDist"  # drawing view (typed FeaturePython)
  Rotation = 0
  ViewResult = <g> \n  <line x1="115.575000" y1="84.675000" x2="149.535514" y2="84.675000" style="stroke:rgb(0,0,255);stroke-width:0.50" />\n<line x1="132.473625" y1="92.464400" x2="149.535514" y2="92.464400" style="stroke:rgb(0,0,255);stroke-width:0.50" />\n<line x1="148.535514" y1="84.675000" x2="148.535514" y2="92.464400" style="stroke:rgb(0,0,255);stroke-width:0.50" /> \n  <polygon points="148.535514,92.464400 149.535514,90.964400 148.535514,90.464400 147.535514,90.964400" style="fill:rgb(0,0,255);stroke:rgb(0,0,255);stroke-width:0" /><polygon points="148.535514,84.675000 147.535514,86.175000 148.535514,86.675000 149.535514,86.175000" style="fill:rgb(0,0,255);stroke:rgb(0,0,255);stroke-width:0" /> \n  <text x="146.535514" y="88.569700" font-family="inherit" font-size="3.6" fill="rgb(0,0,255)" text-anchor="middle" transform="rotate(-90.000000 146.535514,88.569700)" >1.227</text> </g>
  Visible = true
  X = 0
  Y = 0
  arrowL1 = 1.5
  arrowL2 = 0.5
  arrowW = 2
  arrow_scheme = 0
  autoPlaceOffset = 2
  autoPlaceText = true
  click1_x = 148.536
  click1_y = 89.2779
  click2_x = 148.536
  click2_y = 89.2779
  comma_decimal_place = false
  dimension_line_overshoot = 1
  gap_datum_points = 2
  halfDimension_linear = false
  lineColor = rgb(0,0,255)
  strokeWidth = 0.5
  textFormat_linear = %(value)3.3f
  textRenderer_color = rgb(0,0,255)
  textRenderer_family = inherit
  textRenderer_size = 3.6
  unit_custom_scale = 1
  unit_scheme = 2
FEATURE [Drawing::FeatureViewPython] dim011  label="Spinner VDist from Bottom"  # drawing view (typed FeaturePython)
  Rotation = 0
  ViewResult = <g> \n  <line x1="146.500000" y1="106.900000" x2="138.165831" y2="106.900000" style="stroke:rgb(0,0,255);stroke-width:0.50" />\n<line x1="216.350000" y1="119.600000" x2="138.165831" y2="119.600000" style="stroke:rgb(0,0,255);stroke-width:0.50" />\n<line x1="139.165831" y1="106.900000" x2="139.165831" y2="119.600000" style="stroke:rgb(0,0,255);stroke-width:0.50" /> \n  <polygon points="139.165831,119.600000 140.165831,118.100000 139.165831,117.600000 138.165831,118.100000" style="fill:rgb(0,0,255);stroke:rgb(0,0,255);stroke-width:0" /><polygon points="139.165831,106.900000 138.165831,108.400000 139.165831,108.900000 140.165831,108.400000" style="fill:rgb(0,0,255);stroke:rgb(0,0,255);stroke-width:0" /> \n  <text x="137.165831" y="113.250000" font-family="inherit" font-size="3.6" fill="rgb(0,0,255)" text-anchor="middle" transform="rotate(-90.000000 137.165831,113.250000)" >2</text> </g>
  Visible = true
  X = 0
  Y = 0
  arrowL1 = 1.5
  arrowL2 = 0.5
  arrowW = 2
  arrow_scheme = 0
  autoPlaceOffset = 2
  autoPlaceText = true
  click1_x = 139.166
  click1_y = 114.063
  click2_x = 139.166
  click2_y = 114.063
  comma_decimal_place = false
  dimension_line_overshoot = 1
  gap_datum_points = 2
  halfDimension_linear = false
  lineColor = rgb(0,0,255)
  strokeWidth = 0.5
  textFormat_linear = %(value)3.3f
  textRenderer_color = rgb(0,0,255)
  textRenderer_family = inherit
  textRenderer_size = 3.6
  unit_custom_scale = 1
  unit_scheme = 2
FEATURE [Drawing::FeatureViewPython] dim012  label="JSTK2 VDist"  # drawing view (typed FeaturePython)
  Rotation = 0
  ViewResult = <g> \n  <line x1="163.962500" y1="84.675000" x2="156.654905" y2="84.675000" style="stroke:rgb(0,0,255);stroke-width:0.50" />\n<line x1="216.350000" y1="119.600000" x2="156.654905" y2="119.600000" style="stroke:rgb(0,0,255);stroke-width:0.50" />\n<line x1="157.654905" y1="84.675000" x2="157.654905" y2="119.600000" style="stroke:rgb(0,0,255);stroke-width:0.50" /> \n  <polygon points="157.654905,119.600000 158.654905,118.100000 157.654905,117.600000 156.654905,118.100000" style="fill:rgb(0,0,255);stroke:rgb(0,0,255);stroke-width:0" /><polygon points="157.654905,84.675000 156.654905,86.175000 157.654905,86.675000 158.654905,86.175000" style="fill:rgb(0,0,255);stroke:rgb(0,0,255);stroke-width:0" /> \n  <text x="155.654905" y="102.137500" font-family="inherit" font-size="3.6" fill="rgb(0,0,255)" text-anchor="middle" transform="rotate(-90.000000 155.654905,102.137500)" >5.5</text> </g>
  Visible = true
  X = 0
  Y = 0
  arrowL1 = 1.5
  arrowL2 = 0.5
  arrowW = 2
  arrow_scheme = 0
  autoPlaceOffset = 2
  autoPlaceText = true
  click1_x = 157.655
  click1_y = 96.5709
  click2_x = 157.655
  click2_y = 96.5709
  comma_decimal_place = false
  dimension_line_overshoot = 1
  gap_datum_points = 2
  halfDimension_linear = false
  lineColor = rgb(0,0,255)
  strokeWidth = 0.5
  textFormat_linear = %(value)3.3f
  textRenderer_color = rgb(0,0,255)
  textRenderer_family = inherit
  textRenderer_size = 3.6
  unit_custom_scale = 1
  unit_scheme = 2
FEATURE [Drawing::FeatureViewPython] dim013  label="JSTK2 HDist"  # drawing view (typed FeaturePython)
  Rotation = 0
  ViewResult = <g> \n  <line x1="165.962500" y1="86.675000" x2="165.962500" y2="115.750664" style="stroke:rgb(0,0,255);stroke-width:0.50" />\n<line x1="218.350000" y1="117.600000" x2="218.350000" y2="113.750664" style="stroke:rgb(0,0,255);stroke-width:0.50" />\n<line x1="165.962500" y1="114.750664" x2="218.350000" y2="114.750664" style="stroke:rgb(0,0,255);stroke-width:0.50" /> \n  <polygon points="218.350000,114.750664 216.850000,113.750664 216.350000,114.750664 216.850000,115.750664" style="fill:rgb(0,0,255);stroke:rgb(0,0,255);stroke-width:0" /><polygon points="165.962500,114.750664 167.462500,115.750664 167.962500,114.750664 167.462500,113.750664" style="fill:rgb(0,0,255);stroke:rgb(0,0,255);stroke-width:0" /> \n  <text x="192.156250" y="112.750664" font-family="inherit" font-size="3.6" fill="rgb(0,0,255)" text-anchor="middle" transform="rotate(0.000000 192.156250,112.750664)" >8.25</text> </g>
  Visible = true
  X = 0
  Y = 0
  arrowL1 = 1.5
  arrowL2 = 0.5
  arrowW = 2
  arrow_scheme = 0
  autoPlaceOffset = 2
  autoPlaceText = true
  click1_x = 197.214
  click1_y = 114.751
  click2_x = 197.214
  click2_y = 114.751
  comma_decimal_place = false
  dimension_line_overshoot = 1
  gap_datum_points = 2
  halfDimension_linear = false
  lineColor = rgb(0,0,255)
  strokeWidth = 0.5
  textFormat_linear = %(value)3.3f
  textRenderer_color = rgb(0,0,255)
  textRenderer_family = inherit
  textRenderer_size = 3.6
  unit_custom_scale = 1
  unit_scheme = 2
FEATURE [Drawing::FeatureViewPython] dia004  label="JSTK2 Diameter"  # drawing view (typed FeaturePython)
  Rotation = 0
  ViewResult = <g>  <circle cx ="165.962500" cy ="84.675000" r="0.250000" stroke="none" fill="rgb(0,0,255)" /> \n<line x1="166.010814" y1="79.594226" x2="165.932310" y2="87.849856" style="stroke:rgb(0,0,255);stroke-width:0.50" />\n<polygon points="165.992690,81.500144 164.978472,82.990567 165.973673,83.500053 166.978382,83.009584" style="fill:rgb(0,0,255);stroke:rgb(0,0,255);stroke-width:0" />\n<polygon points="165.932310,87.849856 166.946528,86.359433 165.951327,85.849947 164.946618,86.340416" style="fill:rgb(0,0,255);stroke:rgb(0,0,255);stroke-width:0" />\n<line x1="166.010814" y1="79.594226" x2="175.107297" y2="79.594226" style="stroke:rgb(0,0,255);stroke-width:0.50" />\n<text x="170.559055" y="77.594226" font-family="inherit" font-size="3.6" fill="rgb(0,0,255)" text-anchor="middle" transform="rotate(0.000000 170.559055,77.594226)" >Ø1</text> </g>
  Visible = true
  X = 0
  Y = 0
  arrowL1 = 1.5
  arrowL2 = 0.5
  arrowW = 2
  arrow_scheme = 0
  autoPlaceOffset = 2
  autoPlaceText = true
  centerPointDia = 0.5
  click1_x = 166.011
  click1_y = 79.5942
  click2_x = 175.107
  click2_y = 79.8216
  click3_x = 175.107
  click3_y = 79.8216
  comma_decimal_place = false
  lineColor = rgb(0,0,255)
  strokeWidth = 0.5
  textFormat_circular = Ø%(value)3.3f
  textRenderer_color = rgb(0,0,255)
  textRenderer_family = inherit
  textRenderer_size = 3.6
  unit_custom_scale = 1
  unit_scheme = 2
FEATURE [Drawing::FeatureViewPython] dim014  label="P2 Button1 HDist"  # drawing view (typed FeaturePython)
  Rotation = 0
  ViewResult = <g> \n  <line x1="185.012500" y1="94.464400" x2="185.012500" y2="108.168376" style="stroke:rgb(0,0,255);stroke-width:0.50" />\n<line x1="218.350000" y1="117.600000" x2="218.350000" y2="106.168376" style="stroke:rgb(0,0,255);stroke-width:0.50" />\n<line x1="185.012500" y1="107.168376" x2="218.350000" y2="107.168376" style="stroke:rgb(0,0,255);stroke-width:0.50" /> \n  <polygon points="218.350000,107.168376 216.850000,106.168376 216.350000,107.168376 216.850000,108.168376" style="fill:rgb(0,0,255);stroke:rgb(0,0,255);stroke-width:0" /><polygon points="185.012500,107.168376 186.512500,108.168376 187.012500,107.168376 186.512500,106.168376" style="fill:rgb(0,0,255);stroke:rgb(0,0,255);stroke-width:0" /> \n  <text x="201.681250" y="105.168376" font-family="inherit" font-size="3.6" fill="rgb(0,0,255)" text-anchor="middle" transform="rotate(0.000000 201.681250,105.168376)" >5.25</text> </g>
  Visible = true
  X = 0
  Y = 0
  arrowL1 = 1.5
  arrowL2 = 0.5
  arrowW = 2
  arrow_scheme = 0
  autoPlaceOffset = 2
  autoPlaceText = true
  click1_x = 194.031
  click1_y = 107.168
  click2_x = 194.031
  click2_y = 107.168
  comma_decimal_place = false
  dimension_line_overshoot = 1
  gap_datum_points = 2
  halfDimension_linear = false
  lineColor = rgb(0,0,255)
  strokeWidth = 0.5
  textFormat_linear = %(value)3.3f
  textRenderer_color = rgb(0,0,255)
  textRenderer_family = inherit
  textRenderer_size = 3.6
  unit_custom_scale = 1
  unit_scheme = 2
FEATURE [Drawing::FeatureViewPython] dim015  label="P2 Button1 VDist"  # drawing view (typed FeaturePython)
  Rotation = 0
  ViewResult = <g> \n  <line x1="183.012500" y1="92.464400" x2="174.229695" y2="92.464400" style="stroke:rgb(0,0,255);stroke-width:0.50" />\n<line x1="216.350000" y1="119.600000" x2="174.229695" y2="119.600000" style="stroke:rgb(0,0,255);stroke-width:0.50" />\n<line x1="175.229695" y1="92.464400" x2="175.229695" y2="119.600000" style="stroke:rgb(0,0,255);stroke-width:0.50" /> \n  <polygon points="175.229695,119.600000 176.229695,118.100000 175.229695,117.600000 174.229695,118.100000" style="fill:rgb(0,0,255);stroke:rgb(0,0,255);stroke-width:0" /><polygon points="175.229695,92.464400 174.229695,93.964400 175.229695,94.464400 176.229695,93.964400" style="fill:rgb(0,0,255);stroke:rgb(0,0,255);stroke-width:0" /> \n  <text x="173.229695" y="106.032200" font-family="inherit" font-size="3.6" fill="rgb(0,0,255)" text-anchor="middle" transform="rotate(-90.000000 173.229695,106.032200)" >4.273</text> </g>
  Visible = true
  X = 0
  Y = 0
  arrowL1 = 1.5
  arrowL2 = 0.5
  arrowW = 2
  arrow_scheme = 0
  autoPlaceOffset = 2
  autoPlaceText = true
  click1_x = 175.23
  click1_y = 93.4433
  click2_x = 175.23
  click2_y = 93.4433
  comma_decimal_place = false
  dimension_line_overshoot = 1
  gap_datum_points = 2
  halfDimension_linear = false
  lineColor = rgb(0,0,255)
  strokeWidth = 0.5
  textFormat_linear = %(value)3.3f
  textRenderer_color = rgb(0,0,255)
  textRenderer_family = inherit
  textRenderer_size = 3.6
  unit_custom_scale = 1
  unit_scheme = 2
FEATURE [Drawing::FeatureViewPython] dim016  label="P2 Button1 to P2 Button2 VDist"  # drawing view (typed FeaturePython)
  Rotation = 0
  ViewResult = <g> \n  <line x1="183.012500" y1="92.464400" x2="174.262737" y2="92.464400" style="stroke:rgb(0,0,255);stroke-width:0.50" />\n<line x1="190.607500" y1="86.716075" x2="174.262737" y2="86.716075" style="stroke:rgb(0,0,255);stroke-width:0.50" />\n<line x1="175.262737" y1="92.464400" x2="175.262737" y2="86.716075" style="stroke:rgb(0,0,255);stroke-width:0.50" /> \n  <polygon points="175.262737,86.716075 174.262737,88.216075 175.262737,88.716075 176.262737,88.216075" style="fill:rgb(0,0,255);stroke:rgb(0,0,255);stroke-width:0" /><polygon points="175.262737,92.464400 176.262737,90.964400 175.262737,90.464400 174.262737,90.964400" style="fill:rgb(0,0,255);stroke:rgb(0,0,255);stroke-width:0" /> \n  <text x="173.262737" y="89.590238" font-family="inherit" font-size="3.6" fill="rgb(0,0,255)" text-anchor="middle" transform="rotate(-90.000000 173.262737,89.590238)" >0.905</text> </g>
  Visible = true
  X = 0
  Y = 0
  arrowL1 = 1.5
  arrowL2 = 0.5
  arrowW = 2
  arrow_scheme = 0
  autoPlaceOffset = 2
  autoPlaceText = true
  click1_x = 175.263
  click1_y = 88.306
  click2_x = 175.263
  click2_y = 88.306
  comma_decimal_place = false
  dimension_line_overshoot = 1
  gap_datum_points = 2
  halfDimension_linear = false
  lineColor = rgb(0,0,255)
  strokeWidth = 0.5
  textFormat_linear = %(value)3.3f
  textRenderer_color = rgb(0,0,255)
  textRenderer_family = inherit
  textRenderer_size = 3.6
  unit_custom_scale = 1
  unit_scheme = 2
FEATURE [Drawing::FeatureViewPython] dim018  label="P2 Button1 to P2 Button2 HDist"  # drawing view (typed FeaturePython)
  Rotation = 0
  ViewResult = <g> \n  <line x1="185.012500" y1="90.464400" x2="185.012500" y2="74.273156" style="stroke:rgb(0,0,255);stroke-width:0.50" />\n<line x1="192.607500" y1="84.716075" x2="192.607500" y2="74.273156" style="stroke:rgb(0,0,255);stroke-width:0.50" />\n<line x1="185.012500" y1="75.273156" x2="192.607500" y2="75.273156" style="stroke:rgb(0,0,255);stroke-width:0.50" /> \n  <polygon points="192.607500,75.273156 191.107500,74.273156 190.607500,75.273156 191.107500,76.273156" style="fill:rgb(0,0,255);stroke:rgb(0,0,255);stroke-width:0" /><polygon points="185.012500,75.273156 186.512500,76.273156 187.012500,75.273156 186.512500,74.273156" style="fill:rgb(0,0,255);stroke:rgb(0,0,255);stroke-width:0" /> \n  <text x="188.810000" y="73.273156" font-family="inherit" font-size="3.6" fill="rgb(0,0,255)" text-anchor="middle" transform="rotate(0.000000 188.810000,73.273156)" >1.196</text> </g>
  Visible = true
  X = 0
  Y = 0
  arrowL1 = 1.5
  arrowL2 = 0.5
  arrowW = 2
  arrow_scheme = 0
  autoPlaceOffset = 2
  autoPlaceText = true
  click1_x = 192.229
  click1_y = 75.2732
  click2_x = 192.229
  click2_y = 75.2732
  comma_decimal_place = false
  dimension_line_overshoot = 1
  gap_datum_points = 2
  halfDimension_linear = false
  lineColor = rgb(0,0,255)
  strokeWidth = 0.5
  textFormat_linear = %(value)3.3f
  textRenderer_color = rgb(0,0,255)
  textRenderer_family = inherit
  textRenderer_size = 3.6
  unit_custom_scale = 1
  unit_scheme = 2
FEATURE [Drawing::FeatureViewPython] dim019  label="P2 Button2 to P2 Button3 HDist"  # drawing view (typed FeaturePython)
  Rotation = 0
  ViewResult = <g> \n  <line x1="192.607500" y1="84.716075" x2="192.607500" y2="77.632201" style="stroke:rgb(0,0,255);stroke-width:0.50" />\n<line x1="201.911250" y1="82.675000" x2="201.911250" y2="77.632201" style="stroke:rgb(0,0,255);stroke-width:0.50" />\n<line x1="192.607500" y1="78.632201" x2="201.911250" y2="78.632201" style="stroke:rgb(0,0,255);stroke-width:0.50" /> \n  <polygon points="201.911250,78.632201 200.411250,77.632201 199.911250,78.632201 200.411250,79.632201" style="fill:rgb(0,0,255);stroke:rgb(0,0,255);stroke-width:0" /><polygon points="192.607500,78.632201 194.107500,79.632201 194.607500,78.632201 194.107500,77.632201" style="fill:rgb(0,0,255);stroke:rgb(0,0,255);stroke-width:0" /> \n  <text x="197.259375" y="76.632201" font-family="inherit" font-size="3.6" fill="rgb(0,0,255)" text-anchor="middle" transform="rotate(0.000000 197.259375,76.632201)" >1.465</text> </g>
  Visible = true
  X = 0
  Y = 0
  arrowL1 = 1.5
  arrowL2 = 0.5
  arrowW = 2
  arrow_scheme = 0
  autoPlaceOffset = 2
  autoPlaceText = true
  click1_x = 199.711
  click1_y = 78.6322
  click2_x = 199.711
  click2_y = 78.6322
  comma_decimal_place = false
  dimension_line_overshoot = 1
  gap_datum_points = 2
  halfDimension_linear = false
  lineColor = rgb(0,0,255)
  strokeWidth = 0.5
  textFormat_linear = %(value)3.3f
  textRenderer_color = rgb(0,0,255)
  textRenderer_family = inherit
  textRenderer_size = 3.6
  unit_custom_scale = 1
  unit_scheme = 2
FEATURE [Drawing::FeatureViewPython] dim017  label="P2 Button2 to P2 Button3 VDist"  # drawing view (typed FeaturePython)
  Rotation = 0
  ViewResult = <g> \n  <line x1="194.607500" y1="86.716075" x2="213.531811" y2="86.716075" style="stroke:rgb(0,0,255);stroke-width:0.50" />\n<line x1="203.911250" y1="84.675000" x2="213.531811" y2="84.675000" style="stroke:rgb(0,0,255);stroke-width:0.50" />\n<line x1="212.531811" y1="86.716075" x2="212.531811" y2="84.675000" style="stroke:rgb(0,0,255);stroke-width:0.50" /> \n  <polygon points="212.531811,84.675000 213.531811,83.175000 212.531811,82.675000 211.531811,83.175000" style="fill:rgb(0,0,255);stroke:rgb(0,0,255);stroke-width:0" /><polygon points="212.531811,86.716075 211.531811,88.216075 212.531811,88.716075 213.531811,88.216075" style="fill:rgb(0,0,255);stroke:rgb(0,0,255);stroke-width:0" /> \n  <text x="210.531811" y="85.695538" font-family="inherit" font-size="3.6" fill="rgb(0,0,255)" text-anchor="middle" transform="rotate(-90.000000 210.531811,85.695538)" >0.321</text> </g>
  Visible = true
  X = 0
  Y = 0
  arrowL1 = 1.5
  arrowL2 = 0.5
  arrowW = 2
  arrow_scheme = 0
  autoPlaceOffset = 2
  autoPlaceText = true
  click1_x = 212.532
  click1_y = 85.9603
  click2_x = 212.532
  click2_y = 85.9603
  comma_decimal_place = false
  dimension_line_overshoot = 1
  gap_datum_points = 2
  halfDimension_linear = false
  lineColor = rgb(0,0,255)
  strokeWidth = 0.5
  textFormat_linear = %(value)3.3f
  textRenderer_color = rgb(0,0,255)
  textRenderer_family = inherit
  textRenderer_size = 3.6
  unit_custom_scale = 1
  unit_scheme = 2
FEATURE [Drawing::FeatureViewPython] dia005  label="Tab Button Diameter"  # drawing view (typed FeaturePython)
  Rotation = 0
  ViewResult = <g>  <circle cx ="208.825000" cy ="52.925000" r="0.250000" stroke="none" fill="rgb(0,0,255)" /> \n<line x1="208.947076" y1="41.136456" x2="208.788014" y2="56.496683" style="stroke:rgb(0,0,255);stroke-width:0.50" />\n<polygon points="208.861986,49.353317 207.846508,50.842881 208.841277,51.353209 209.846400,50.863591" style="fill:rgb(0,0,255);stroke:rgb(0,0,255);stroke-width:0" />\n<polygon points="208.788014,56.496683 209.803492,55.007119 208.808723,54.496791 207.803600,54.986409" style="fill:rgb(0,0,255);stroke:rgb(0,0,255);stroke-width:0" />\n<line x1="208.947076" y1="41.136456" x2="200.785081" y2="41.136456" style="stroke:rgb(0,0,255);stroke-width:0.50" />\n<text x="204.866078" y="39.136456" font-family="inherit" font-size="3.6" fill="rgb(0,0,255)" text-anchor="middle" transform="rotate(0.000000 204.866078,39.136456)" >Ø1.125</text> </g>
  Visible = true
  X = 0
  Y = 0
  arrowL1 = 1.5
  arrowL2 = 0.5
  arrowW = 2
  arrow_scheme = 0
  autoPlaceOffset = 2
  autoPlaceText = true
  centerPointDia = 0.5
  click1_x = 208.947
  click1_y = 41.1365
  click2_x = 200.785
  click2_y = 40.81
  click3_x = 200.785
  click3_y = 40.81
  comma_decimal_place = false
  lineColor = rgb(0,0,255)
  strokeWidth = 0.5
  textFormat_circular = Ø%(value)3.3f
  textRenderer_color = rgb(0,0,255)
  textRenderer_family = inherit
  textRenderer_size = 3.6
  unit_custom_scale = 1
  unit_scheme = 2
FEATURE [Drawing::FeatureViewPython] dim021  label="Tab Button HDist"  # drawing view (typed FeaturePython)
  Rotation = 0
  ViewResult = <g> \n  <line x1="208.825000" y1="54.925000" x2="208.825000" y2="63.847363" style="stroke:rgb(0,0,255);stroke-width:0.50" />\n<line x1="218.350000" y1="45.400000" x2="218.350000" y2="63.847363" style="stroke:rgb(0,0,255);stroke-width:0.50" />\n<line x1="208.825000" y1="62.847363" x2="218.350000" y2="62.847363" style="stroke:rgb(0,0,255);stroke-width:0.50" /> \n  <polygon points="218.350000,62.847363 216.850000,61.847363 216.350000,62.847363 216.850000,63.847363" style="fill:rgb(0,0,255);stroke:rgb(0,0,255);stroke-width:0" /><polygon points="208.825000,62.847363 210.325000,63.847363 210.825000,62.847363 210.325000,61.847363" style="fill:rgb(0,0,255);stroke:rgb(0,0,255);stroke-width:0" /> \n  <text x="213.587500" y="60.847363" font-family="inherit" font-size="3.6" fill="rgb(0,0,255)" text-anchor="middle" transform="rotate(0.000000 213.587500,60.847363)" >1.5</text> </g>
  Visible = true
  X = 0
  Y = 0
  arrowL1 = 1.5
  arrowL2 = 0.5
  arrowW = 2
  arrow_scheme = 0
  autoPlaceOffset = 2
  autoPlaceText = true
  click1_x = 209.437
  click1_y = 62.8474
  click2_x = 209.437
  click2_y = 62.8474
  comma_decimal_place = false
  dimension_line_overshoot = 1
  gap_datum_points = 2
  halfDimension_linear = false
  lineColor = rgb(0,0,255)
  strokeWidth = 0.5
  textFormat_linear = %(value)3.3f
  textRenderer_color = rgb(0,0,255)
  textRenderer_family = inherit
  textRenderer_size = 3.6
  unit_custom_scale = 1
  unit_scheme = 2
FEATURE [Drawing::FeatureViewPython] dim020  label="Tab Button VDist"  # drawing view (typed FeaturePython)
  Rotation = 0
  ViewResult = <g> \n  <line x1="206.825000" y1="52.925000" x2="199.458703" y2="52.925000" style="stroke:rgb(0,0,255);stroke-width:0.50" />\n<line x1="216.350000" y1="43.400000" x2="199.458703" y2="43.400000" style="stroke:rgb(0,0,255);stroke-width:0.50" />\n<line x1="200.458703" y1="52.925000" x2="200.458703" y2="43.400000" style="stroke:rgb(0,0,255);stroke-width:0.50" /> \n  <polygon points="200.458703,43.400000 199.458703,44.900000 200.458703,45.400000 201.458703,44.900000" style="fill:rgb(0,0,255);stroke:rgb(0,0,255);stroke-width:0" /><polygon points="200.458703,52.925000 201.458703,51.425000 200.458703,50.925000 199.458703,51.425000" style="fill:rgb(0,0,255);stroke:rgb(0,0,255);stroke-width:0" /> \n  <text x="198.458703" y="48.162500" font-family="inherit" font-size="3.6" fill="rgb(0,0,255)" text-anchor="middle" transform="rotate(-90.000000 198.458703,48.162500)" >1.5</text> </g>
  Visible = true
  X = 0
  Y = 0
  arrowL1 = 1.5
  arrowL2 = 0.5
  arrowW = 2
  arrow_scheme = 0
  autoPlaceOffset = 2
  autoPlaceText = true
  click1_x = 200.459
  click1_y = 52.032
  click2_x = 200.459
  click2_y = 52.032
  comma_decimal_place = false
  dimension_line_overshoot = 1
  gap_datum_points = 2
  halfDimension_linear = false
  lineColor = rgb(0,0,255)
  strokeWidth = 0.5
  textFormat_linear = %(value)3.3f
  textRenderer_color = rgb(0,0,255)
  textRenderer_family = inherit
  textRenderer_size = 3.6
  unit_custom_scale = 1
  unit_scheme = 2
FEATURE [Drawing::FeatureViewPython] dia006  label="Spinner Diameter"  # drawing view (typed FeaturePython)
  Rotation = 0
  ViewResult = <g>  <circle cx ="148.500000" cy ="106.900000" r="0.250000" stroke="none" fill="rgb(0,0,255)" /> \n<line x1="148.609364" y1="101.763914" x2="148.415512" y2="110.867851" style="stroke:rgb(0,0,255);stroke-width:0.50" />\n<polygon points="148.584488,102.932149 147.552782,104.410521 148.541912,104.931696 149.552329,104.453098" style="fill:rgb(0,0,255);stroke:rgb(0,0,255);stroke-width:0" />\n<polygon points="148.415512,110.867851 149.447218,109.389479 148.458088,108.868304 147.447671,109.346902" style="fill:rgb(0,0,255);stroke:rgb(0,0,255);stroke-width:0" />\n<line x1="148.609364" y1="101.763914" x2="138.394529" y2="101.763914" style="stroke:rgb(0,0,255);stroke-width:0.50" />\n<text x="143.501947" y="99.763914" font-family="inherit" font-size="3.6" fill="rgb(0,0,255)" text-anchor="middle" transform="rotate(0.000000 143.501947,99.763914)" >Ø1.25</text> </g>
  Visible = true
  X = 0
  Y = 0
  arrowL1 = 1.5
  arrowL2 = 0.5
  arrowW = 2
  arrow_scheme = 0
  autoPlaceOffset = 2
  autoPlaceText = true
  centerPointDia = 0.5
  click1_x = 148.609
  click1_y = 101.764
  click2_x = 138.395
  click2_y = 102.148
  click3_x = 138.395
  click3_y = 102.148
  comma_decimal_place = false
  lineColor = rgb(0,0,255)
  strokeWidth = 0.5
  textFormat_circular = Ø%(value)3.3f
  textRenderer_color = rgb(0,0,255)
  textRenderer_family = inherit
  textRenderer_size = 3.6
  unit_custom_scale = 1
  unit_scheme = 2
FEATURE [Drawing::FeaturePage] Page  label="Control Panel Drawing"
  EditableTexts = Aaron Lim | 11 APR 2020 | 1in/1mm | N/A | Arcade Cabinet | Control Panel | V2.0 | 01
  Group = -> [Ortho,dim001,dim002,dim004,dim005,dim006,dim008,dim009,dim010,dia001,dia002,dia003,dimStack001,dimStack002,centerLines001,centerLines002,centerLines003,centerLines004,dim003,dim007,dim011,dim012,dim013,dia004,dim014,dim015,dim016,dim018,dim019,dim017,dia005,dim021,dim020,dia006]
  Template = /Applications/FreeCAD.app/Contents/Resources/data/Mod/Drawing/Templates/A4_Landscape.svg
FEATURE [App::DocumentObjectGroup] Group  label="Control Panel"
  Group = -> [Body,Page]
